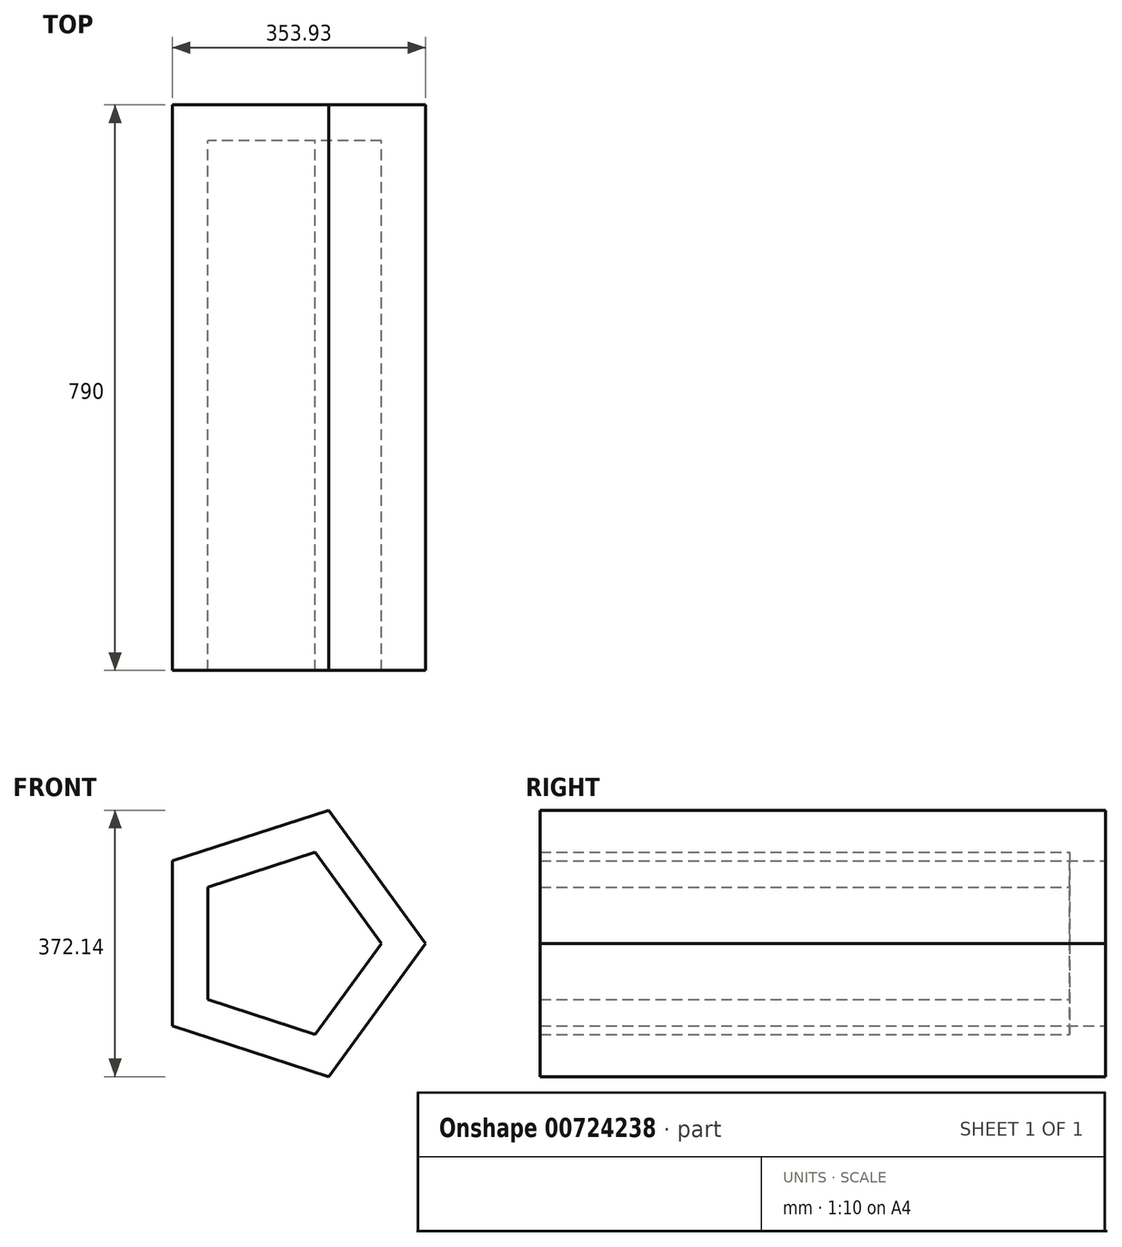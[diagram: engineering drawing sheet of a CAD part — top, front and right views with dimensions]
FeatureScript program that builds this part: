
annotation { "Feature Type Name" : "Feature", "Feature Type Description" : "" }
export const myFeature = defineFeature(function(context is Context, id is Id, definition is map)
    precondition{}
    {
        {
            var Q0;
            Q0=qCreatedBy(makeId("Front.planeOp"),FACE);
            var sketch = newSketch(context, id + "F0", { "sketchPlane" : qUnion([Q0])});
            skCircle(sketch, "E0.cCircle", {"center": v(0, 0) * mm, "radius": 158.28 * mm, "construction": true});
            skLineSegment(sketch, "E0.0", {"start": v(-158.28, -115) * mm, "end": v(-158.28, 115) * mm});
            skLineSegment(sketch, "E0.1", {"start": v(-158.28, 115) * mm, "end": v(60.46, 186.07) * mm});
            skLineSegment(sketch, "E0.2", {"start": v(60.46, 186.07) * mm, "end": v(195.65, 0) * mm});
            skLineSegment(sketch, "E0.3", {"start": v(195.65, 0) * mm, "end": v(60.46, -186.07) * mm});
            skLineSegment(sketch, "E0.4", {"start": v(60.46, -186.07) * mm, "end": v(-158.28, -115) * mm});
            skPoint(sketch, "E0.0.midPoint", {"position": v(-158.28, 0) * mm});
            skLineSegment(sketch, "E1", {"start": v(-158.28, 115) * mm, "end": v(-158.28, -115) * mm});
            skSolve(sketch);
        }
        {
            var Q0;
            Q0 = qSketchRegion(id + "F0", true);
            extrude(context, id + "F1", {"entities" : qUnion([Q0]), "depth" : 790 * mm, "offsetDistance" : 25.4 * mm});
        }
        {
            var Q0;
            Q0=makeQuery(id+"F1.opExtrude","CAP_FACE",FACE,{"disambiguationData":[OSD([sQuery(id+"F0.wireOp",EDGE,"E0.0"),sQuery(id+"F0.wireOp",EDGE,"E0.1"),sQuery(id+"F0.wireOp",EDGE,"E0.2"),sQuery(id+"F0.wireOp",EDGE,"E0.3"),sQuery(id+"F0.wireOp",EDGE,"E0.4")])],"isStart":false});
            shell(context, id + "F2", {"entities" : qUnion([Q0]), "thickness" : 50 * mm});
        }
    });
